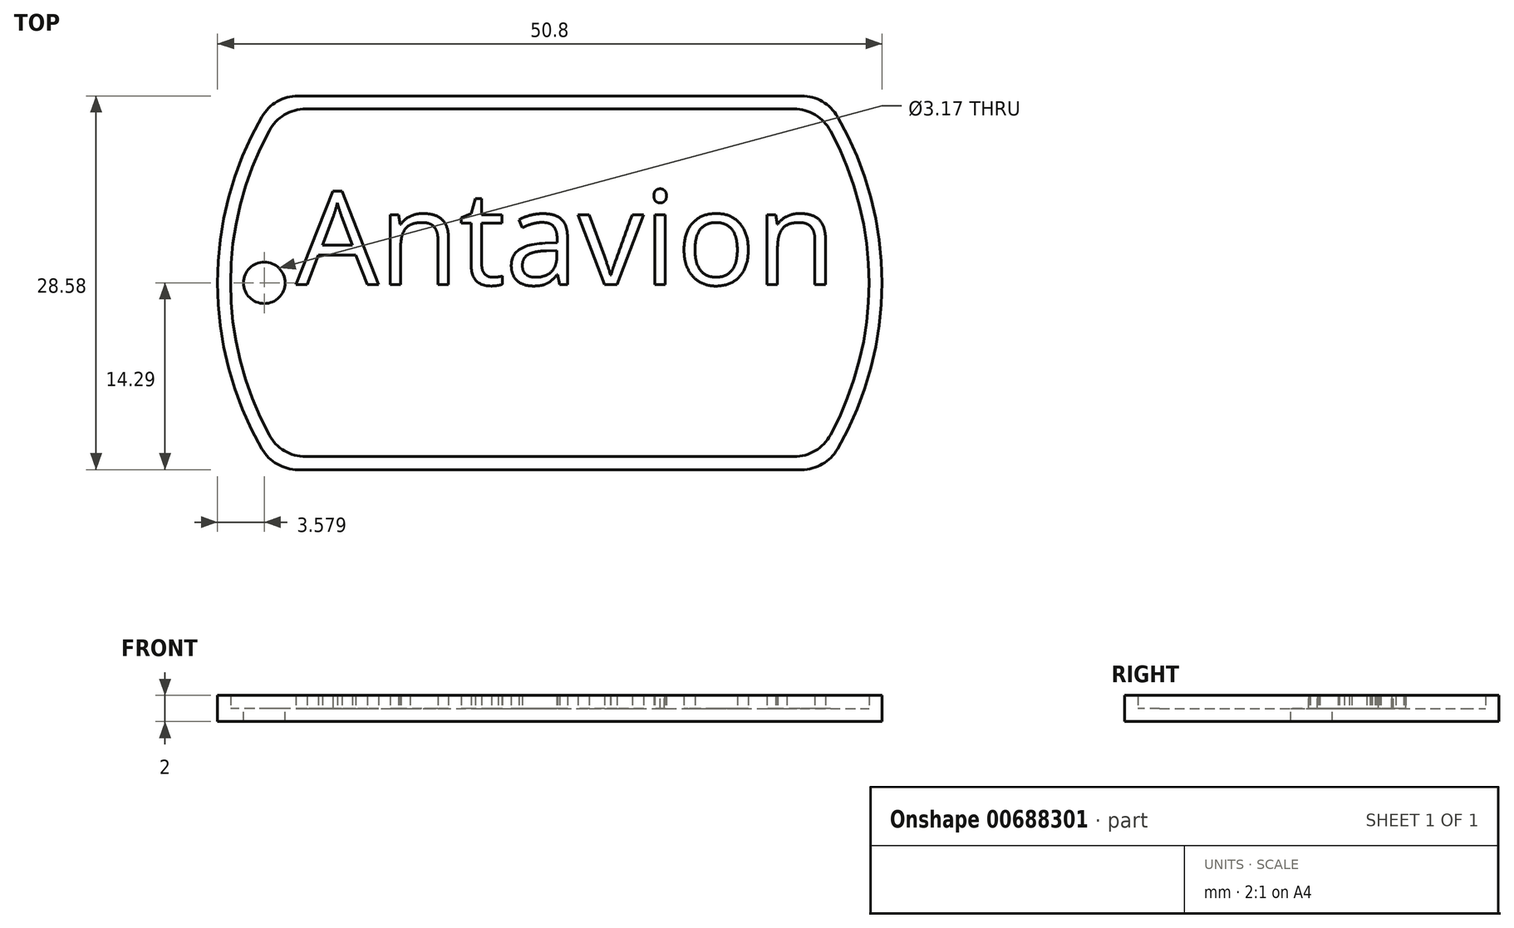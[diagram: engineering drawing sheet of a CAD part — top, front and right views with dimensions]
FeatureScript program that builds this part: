
annotation { "Feature Type Name" : "Feature", "Feature Type Description" : "" }
export const myFeature = defineFeature(function(context is Context, id is Id, definition is map)
    precondition{}
    {
        {
            var Q0;
            Q0=qCreatedBy(makeId("Top.planeOp"),FACE);
            var sketch = newSketch(context, id + "F0", { "sketchPlane" : qUnion([Q0])});
            skArc(sketch, "E0", {"start": v(-22, 12.7) * mm, "mid": v(-25.4, 0) * mm, "end": v(-22, -12.7) * mm});
            skLineSegment(sketch, "E1.top", {"start": v(-19.25, -14.29) * mm, "end": v(19.25, -14.29) * mm});
            skArc(sketch, "E2.trimOffspring", {"start": v(22, -12.7) * mm, "mid": v(25.4, 0) * mm, "end": v(22, 12.7) * mm});
            skLineSegment(sketch, "E3", {"start": v(-19.25, 14.29) * mm, "end": v(19.25, 14.29) * mm});
            skPoint(sketch, "E4.visualSharp", {"position": v(-21, 14.29) * mm});
            skArc(sketch, "E4.filletArc", {"start": v(-19.25, 14.29) * mm, "mid": v(-20.83, 13.86) * mm, "end": v(-22, 12.7) * mm});
            skPoint(sketch, "E5.visualSharp", {"position": v(21, 14.29) * mm});
            skArc(sketch, "E5.filletArc", {"start": v(22, 12.7) * mm, "mid": v(20.83, 13.86) * mm, "end": v(19.25, 14.29) * mm});
            skPoint(sketch, "E6.visualSharp", {"position": v(21, -14.29) * mm});
            skArc(sketch, "E6.filletArc", {"start": v(19.25, -14.29) * mm, "mid": v(20.83, -13.86) * mm, "end": v(22, -12.7) * mm});
            skPoint(sketch, "E7.visualSharp", {"position": v(-21, -14.29) * mm});
            skArc(sketch, "E7.filletArc", {"start": v(-22, -12.7) * mm, "mid": v(-20.83, -13.86) * mm, "end": v(-19.25, -14.29) * mm});
            skSolve(sketch);
        }
        {
            var Q0;
            Q0=makeQuery(id+"F0.imprint","IMPRINT",FACE,{"disambiguationData":[TD([[makeQuery(id+"F0.imprint","IMPRINT",EDGE,{"derivedFrom":sQuery(id+"F0.wireOp",EDGE,"E0")}),1.0]])]});
            extrude(context, id + "F1", {"entities" : qUnion([Q0]), "depth" : 1 * mm, "offsetDistance" : 25.4 * mm});
        }
        {
            var Q0;
            Q0=makeQuery(id+"F1.opExtrude","CAP_FACE",FACE,{"disambiguationData":[OSD([sQuery(id+"F0.wireOp",EDGE,"E0"),sQuery(id+"F0.wireOp",EDGE,"E1.top"),sQuery(id+"F0.wireOp",EDGE,"E2.trimOffspring"),sQuery(id+"F0.wireOp",EDGE,"E3"),sQuery(id+"F0.wireOp",EDGE,"E4.filletArc"),sQuery(id+"F0.wireOp",EDGE,"E5.filletArc"),sQuery(id+"F0.wireOp",EDGE,"E6.filletArc"),sQuery(id+"F0.wireOp",EDGE,"E7.filletArc")])],"isStart":false});
            var sketch = newSketch(context, id + "F2", { "sketchPlane" : qUnion([Q0])});
            skLineSegment(sketch, "E8.0", {"start": v(-18.66, 13.29) * mm, "end": v(18.66, 13.29) * mm});
            skArc(sketch, "E8.1", {"start": v(-21.45, 11.63) * mm, "mid": v(-24.4, 0) * mm, "end": v(-21.45, -11.63) * mm});
            skLineSegment(sketch, "E8.2", {"start": v(-18.66, -13.29) * mm, "end": v(18.66, -13.29) * mm});
            skArc(sketch, "E8.3", {"start": v(21.45, -11.63) * mm, "mid": v(24.4, 0) * mm, "end": v(21.45, 11.63) * mm});
            skPoint(sketch, "E9.visualSharp", {"position": v(-20.46, 13.29) * mm});
            skArc(sketch, "E9.filletArc", {"start": v(-18.66, 13.29) * mm, "mid": v(-20.29, 12.84) * mm, "end": v(-21.45, 11.63) * mm});
            skPoint(sketch, "E10.visualSharp", {"position": v(20.46, 13.29) * mm});
            skArc(sketch, "E10.filletArc", {"start": v(21.45, 11.63) * mm, "mid": v(20.29, 12.84) * mm, "end": v(18.66, 13.29) * mm});
            skPoint(sketch, "E11.visualSharp", {"position": v(20.46, -13.29) * mm});
            skArc(sketch, "E11.filletArc", {"start": v(18.66, -13.29) * mm, "mid": v(20.29, -12.84) * mm, "end": v(21.45, -11.63) * mm});
            skPoint(sketch, "E12.visualSharp", {"position": v(-20.46, -13.29) * mm});
            skArc(sketch, "E12.filletArc", {"start": v(-21.45, -11.63) * mm, "mid": v(-20.29, -12.84) * mm, "end": v(-18.66, -13.29) * mm});
            skLineSegment(sketch, "E13.0", {"start": v(-19.25, 14.29) * mm, "end": v(19.25, 14.29) * mm});
            skArc(sketch, "E13.1", {"start": v(-22, 12.7) * mm, "mid": v(-25.4, 0) * mm, "end": v(-22, -12.7) * mm});
            skLineSegment(sketch, "E13.2", {"start": v(-19.25, -14.29) * mm, "end": v(19.25, -14.29) * mm});
            skArc(sketch, "E13.3", {"start": v(22, -12.7) * mm, "mid": v(25.4, 0) * mm, "end": v(22, 12.7) * mm});
            skPoint(sketch, "E14.visualSharp", {"position": v(-21, -14.29) * mm});
            skArc(sketch, "E14.filletArc", {"start": v(-22, -12.7) * mm, "mid": v(-20.83, -13.86) * mm, "end": v(-19.25, -14.29) * mm});
            skPoint(sketch, "E15.visualSharp", {"position": v(21, -14.29) * mm});
            skArc(sketch, "E15.filletArc", {"start": v(19.25, -14.29) * mm, "mid": v(20.83, -13.86) * mm, "end": v(22, -12.7) * mm});
            skPoint(sketch, "E16.visualSharp", {"position": v(21, 14.29) * mm});
            skArc(sketch, "E16.filletArc", {"start": v(22, 12.7) * mm, "mid": v(20.83, 13.86) * mm, "end": v(19.25, 14.29) * mm});
            skPoint(sketch, "E17.visualSharp", {"position": v(-21, 14.29) * mm});
            skArc(sketch, "E17.filletArc", {"start": v(-19.25, 14.29) * mm, "mid": v(-20.83, 13.86) * mm, "end": v(-22, 12.7) * mm});
            skSolve(sketch);
        }
        {
            var Q0;
            Q0=makeQuery(id+"F2.imprint","IMPRINT",FACE,{"disambiguationData":[TD([[makeQuery(id+"F2.imprint","IMPRINT",EDGE,{"derivedFrom":sQuery(id+"F2.wireOp",EDGE,"E8.0")}),1.0]])]});
            extrude(context, id + "F3", {"entities" : qUnion([Q0]), "operationType" : NewBodyOperationType.ADD, "depth" : 1 * mm, "offsetDistance" : 25.4 * mm});
        }
        {
            var Q0;
            Q0=makeQuery(id+"F1.opExtrude","CAP_FACE",FACE,{"disambiguationData":[OSD([sQuery(id+"F0.wireOp",EDGE,"E0"),sQuery(id+"F0.wireOp",EDGE,"E1.top"),sQuery(id+"F0.wireOp",EDGE,"E2.trimOffspring"),sQuery(id+"F0.wireOp",EDGE,"E3"),sQuery(id+"F0.wireOp",EDGE,"E4.filletArc"),sQuery(id+"F0.wireOp",EDGE,"E5.filletArc"),sQuery(id+"F0.wireOp",EDGE,"E6.filletArc"),sQuery(id+"F0.wireOp",EDGE,"E7.filletArc")])],"isStart":false});
            var sketch = newSketch(context, id + "F4", { "sketchPlane" : qUnion([Q0])});
            skCircle(sketch, "E18", {"center": v(-21.82, 0) * mm, "radius": 1.59 * mm});
            skSolve(sketch);
        }
        {
            var Q0;
            Q0=makeQuery(id+"F4.imprint","IMPRINT",FACE,{"disambiguationData":[TD([[makeQuery(id+"F4.imprint","IMPRINT",EDGE,{"derivedFrom":sQuery(id+"F4.wireOp",EDGE,"E18")}),1.0]])]});
            extrude(context, id + "F5", {"entities" : qUnion([Q0]), "operationType" : NewBodyOperationType.REMOVE, "oppositeDirection" : true, "depth" : 1 * mm, "offsetDistance" : 25.4 * mm});
        }
        {
            var Q0;
            Q0=makeQuery(id+"F2.imprint","IMPRINT",FACE,{"disambiguationData":[TD([[makeQuery(id+"F2.imprint","IMPRINT",EDGE,{"derivedFrom":sQuery(id+"F2.wireOp",EDGE,"E8.0")}),-1.0]])]});
            var sketch = newSketch(context, id + "F6", { "sketchPlane" : qUnion([Q0])});
            skText(sketch, "E19", { "text": "Antavion", "fontName": "OpenSans-Regular.ttf"});
            const initialGuessF6  = {"E19": [-0.0194, -0.00015, 1, 0, 0.0072]};
            skSetInitialGuess(sketch, initialGuessF6);
            skSolve(sketch);
        }
        {
            var Q0;
            Q0 = qSketchRegion(id + "F6", true);
            extrude(context, id + "F7", {"entities" : qUnion([Q0]), "operationType" : NewBodyOperationType.ADD, "depth" : 1 * mm, "offsetDistance" : 25.4 * mm});
        }
    });
